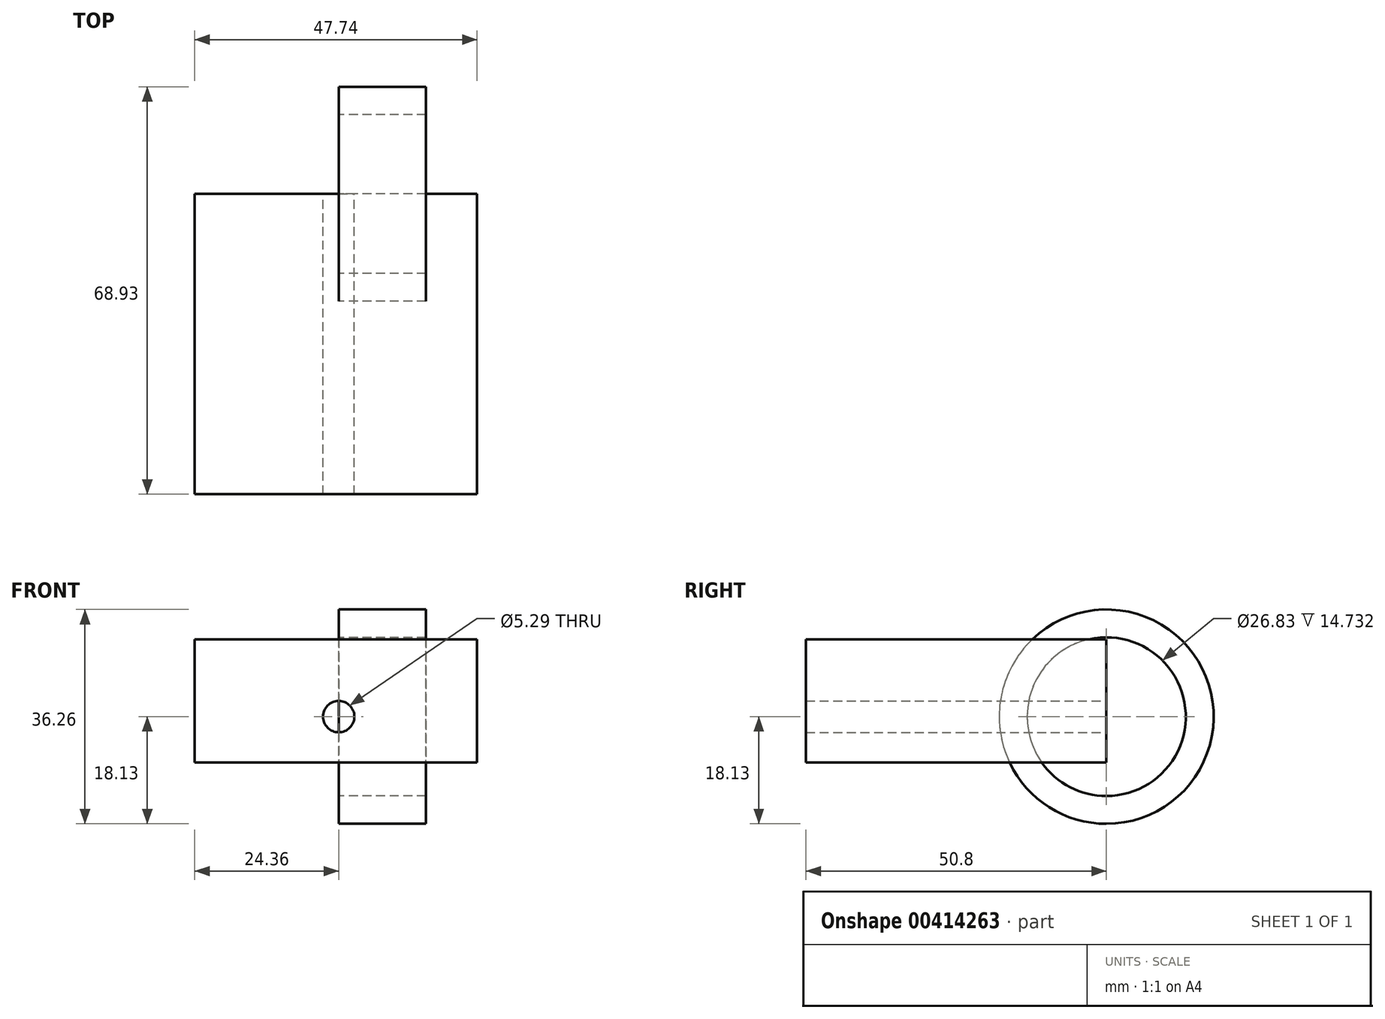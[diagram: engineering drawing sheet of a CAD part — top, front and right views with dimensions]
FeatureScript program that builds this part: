
annotation { "Feature Type Name" : "Feature", "Feature Type Description" : "" }
export const myFeature = defineFeature(function(context is Context, id is Id, definition is map)
    precondition{}
    {
        {
            var Q0;
            Q0=qCreatedBy(makeId("Right.planeOp"),FACE);
            var sketch = newSketch(context, id + "F0", { "sketchPlane" : qUnion([Q0])});
            skCircle(sketch, "E0", {"center": v(0, 0) * mm, "radius": 13.41 * mm});
            skCircle(sketch, "E1", {"center": v(0, 0) * mm, "radius": 18.13 * mm});
            skSolve(sketch);
        }
        {
            var Q0;
            Q0 = qSketchRegion(id + "F0", true);
            extrude(context, id + "F1", {"entities" : qUnion([Q0]), "depth" : 14.73 * mm});
        }
        {
            var Q0;
            Q0=qCreatedBy(makeId("Front.planeOp"),FACE);
            var sketch = newSketch(context, id + "F2", { "sketchPlane" : qUnion([Q0])});
            skLineSegment(sketch, "E2.bottom", {"start": v(23.38, 13.1) * mm, "end": v(-24.36, 13.1) * mm});
            skLineSegment(sketch, "E2.top", {"start": v(23.38, -7.79) * mm, "end": v(-24.36, -7.79) * mm});
            skLineSegment(sketch, "E2.left", {"start": v(23.38, 13.1) * mm, "end": v(23.38, -7.79) * mm});
            skLineSegment(sketch, "E2.right", {"start": v(-24.36, 13.1) * mm, "end": v(-24.36, -7.79) * mm});
            skCircle(sketch, "E3", {"center": v(0, 0) * mm, "radius": 1.85 * mm});
            skCircle(sketch, "E4", {"center": v(0, 0) * mm, "radius": 2.65 * mm});
            skSolve(sketch);
        }
        {
            var Q0;
            Q0 = qSketchRegion(id + "F2", true);
            extrude(context, id + "F3", {"entities" : qUnion([Q0]), "depth" : 25.4 * mm});
        }
        {
            var Q0;
            Q0=makeQuery(id+"F3.opExtrude","CAP_FACE",FACE,{"disambiguationData":[OSD([sQuery(id+"F2.wireOp",EDGE,"E2.bottom"),sQuery(id+"F2.wireOp",EDGE,"E2.top"),sQuery(id+"F2.wireOp",EDGE,"E2.left"),sQuery(id+"F2.wireOp",EDGE,"E2.right"),sQuery(id+"F2.wireOp",EDGE,"E4")])],"isStart":false});
            extrude(context, id + "F4", {"entities" : qUnion([Q0]), "operationType" : NewBodyOperationType.ADD, "depth" : 25.4 * mm});
        }
    });
